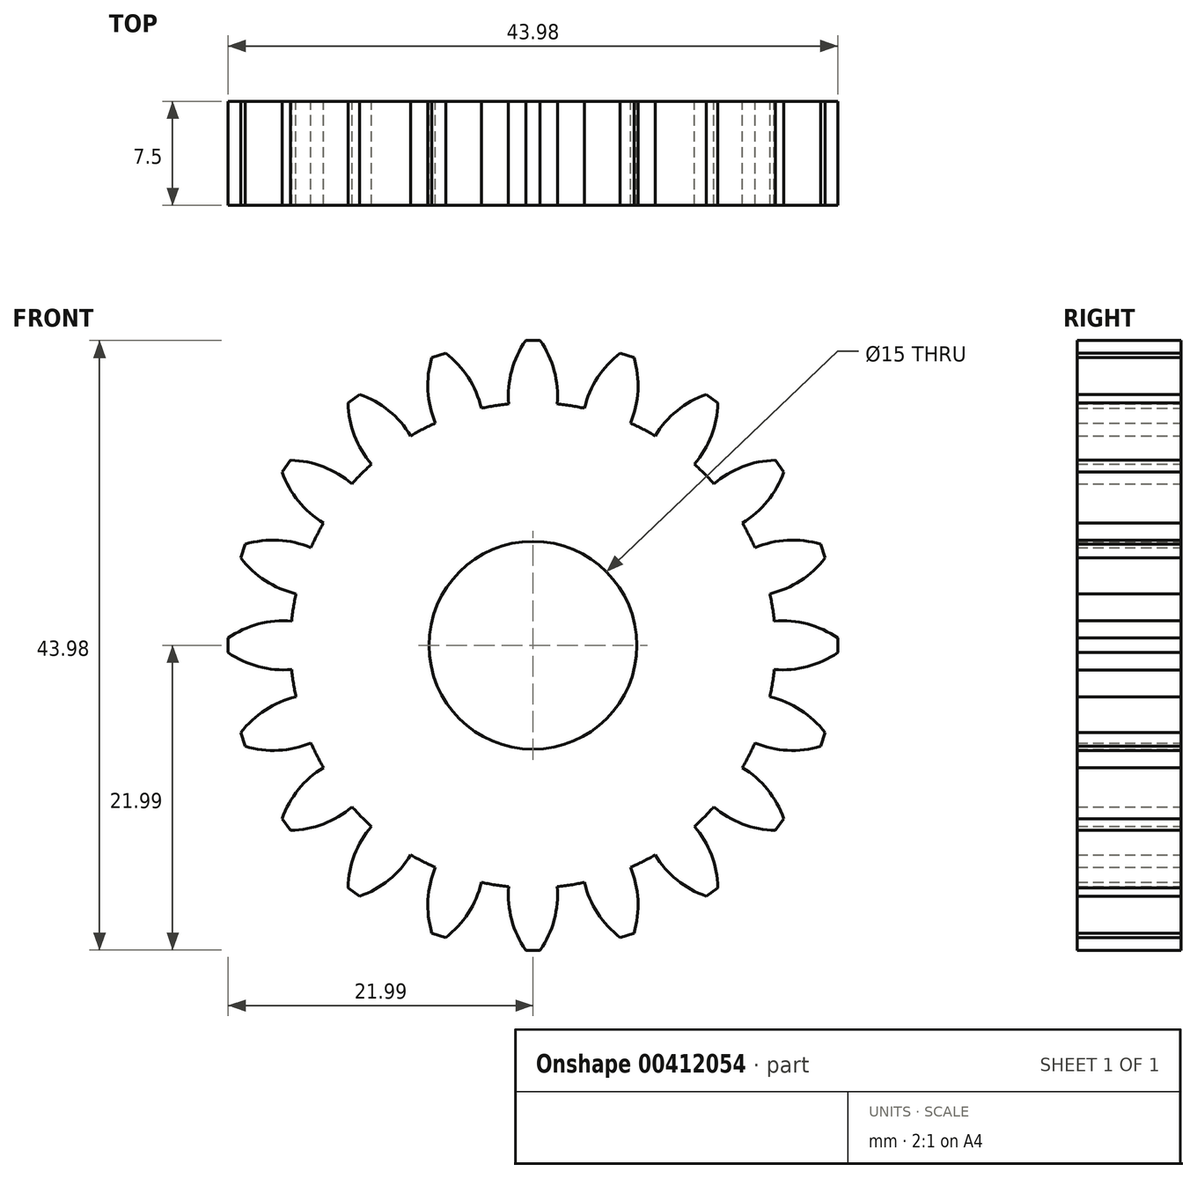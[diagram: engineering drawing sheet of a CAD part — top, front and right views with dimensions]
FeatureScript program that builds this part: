
annotation { "Feature Type Name" : "Feature", "Feature Type Description" : "" }
export const myFeature = defineFeature(function(context is Context, id is Id, definition is map)
    precondition{}
    {
        {
            var Q0;
            Q0=qCreatedBy(makeId("Front.planeOp"),FACE);
            var sketch = newSketch(context, id + "F0", { "sketchPlane" : qUnion([Q0])});
            skCircle(sketch, "E0", {"center": v(0, 0) * mm, "radius": 17.5 * mm});
            skCircle(sketch, "E1", {"center": v(0, 0) * mm, "radius": 22 * mm});
            skCircle(sketch, "E2", {"center": v(0, 0) * mm, "radius": 7.5 * mm});
            skLineSegment(sketch, "E3", {"start": v(-0.52, 22) * mm, "end": v(0.52, 22) * mm});
            skArc(sketch, "E4", {"start": v(-0.52, 22) * mm, "mid": v(-1.53, 19.81) * mm, "end": v(-1.75, 17.41) * mm});
            skArc(sketch, "E5.MirrorCS", {"start": v(0.52, 22) * mm, "mid": v(1.53, 19.81) * mm, "end": v(1.75, 17.41) * mm});
            skLineSegment(sketch, "E6.1.0", {"start": v(-7.3, 20.76) * mm, "end": v(-6.3, 21.08) * mm});
            skArc(sketch, "E6.1.1", {"start": v(-7.3, 20.76) * mm, "mid": v(-7.58, 18.37) * mm, "end": v(-7.04, 16.02) * mm});
            skArc(sketch, "E6.1.2", {"start": v(-6.3, 21.08) * mm, "mid": v(-4.66, 19.31) * mm, "end": v(-3.72, 17.1) * mm});
            skLineSegment(sketch, "E6.2.0", {"start": v(-13.35, 17.49) * mm, "end": v(-12.5, 18.1) * mm});
            skArc(sketch, "E6.2.1", {"start": v(-13.35, 17.49) * mm, "mid": v(-12.88, 15.13) * mm, "end": v(-11.65, 13.06) * mm});
            skArc(sketch, "E6.2.2", {"start": v(-12.5, 18.1) * mm, "mid": v(-10.4, 16.93) * mm, "end": v(-8.82, 15.11) * mm});
            skLineSegment(sketch, "E6.3.0", {"start": v(-18.1, 12.5) * mm, "end": v(-17.49, 13.35) * mm});
            skArc(sketch, "E6.3.1", {"start": v(-18.1, 12.5) * mm, "mid": v(-16.93, 10.4) * mm, "end": v(-15.11, 8.82) * mm});
            skArc(sketch, "E6.3.2", {"start": v(-17.49, 13.35) * mm, "mid": v(-15.13, 12.88) * mm, "end": v(-13.06, 11.65) * mm});
            skLineSegment(sketch, "E6.4.0", {"start": v(-21.08, 6.3) * mm, "end": v(-20.76, 7.3) * mm});
            skArc(sketch, "E6.4.1", {"start": v(-21.08, 6.3) * mm, "mid": v(-19.31, 4.66) * mm, "end": v(-17.1, 3.72) * mm});
            skArc(sketch, "E6.4.2", {"start": v(-20.76, 7.3) * mm, "mid": v(-18.37, 7.58) * mm, "end": v(-16.02, 7.04) * mm});
            skLineSegment(sketch, "E6.5.0", {"start": v(-22, -0.52) * mm, "end": v(-22, 0.52) * mm});
            skArc(sketch, "E6.5.1", {"start": v(-22, -0.52) * mm, "mid": v(-19.81, -1.53) * mm, "end": v(-17.41, -1.75) * mm});
            skArc(sketch, "E6.5.2", {"start": v(-22, 0.52) * mm, "mid": v(-19.81, 1.53) * mm, "end": v(-17.41, 1.75) * mm});
            skLineSegment(sketch, "E6.6.0", {"start": v(-20.76, -7.3) * mm, "end": v(-21.08, -6.3) * mm});
            skArc(sketch, "E6.6.1", {"start": v(-20.76, -7.3) * mm, "mid": v(-18.37, -7.58) * mm, "end": v(-16.02, -7.04) * mm});
            skArc(sketch, "E6.6.2", {"start": v(-21.08, -6.3) * mm, "mid": v(-19.31, -4.66) * mm, "end": v(-17.1, -3.72) * mm});
            skLineSegment(sketch, "E6.7.0", {"start": v(-17.49, -13.35) * mm, "end": v(-18.1, -12.5) * mm});
            skArc(sketch, "E6.7.1", {"start": v(-17.49, -13.35) * mm, "mid": v(-15.13, -12.88) * mm, "end": v(-13.06, -11.65) * mm});
            skArc(sketch, "E6.7.2", {"start": v(-18.1, -12.5) * mm, "mid": v(-16.93, -10.4) * mm, "end": v(-15.11, -8.82) * mm});
            skLineSegment(sketch, "E6.8.0", {"start": v(-12.5, -18.1) * mm, "end": v(-13.35, -17.49) * mm});
            skArc(sketch, "E6.8.1", {"start": v(-12.5, -18.1) * mm, "mid": v(-10.4, -16.93) * mm, "end": v(-8.82, -15.11) * mm});
            skArc(sketch, "E6.8.2", {"start": v(-13.35, -17.49) * mm, "mid": v(-12.88, -15.13) * mm, "end": v(-11.65, -13.06) * mm});
            skLineSegment(sketch, "E6.9.0", {"start": v(-6.3, -21.08) * mm, "end": v(-7.3, -20.76) * mm});
            skArc(sketch, "E6.9.1", {"start": v(-6.3, -21.08) * mm, "mid": v(-4.66, -19.31) * mm, "end": v(-3.72, -17.1) * mm});
            skArc(sketch, "E6.9.2", {"start": v(-7.3, -20.76) * mm, "mid": v(-7.58, -18.37) * mm, "end": v(-7.04, -16.02) * mm});
            skLineSegment(sketch, "E6.10.0", {"start": v(0.52, -22) * mm, "end": v(-0.52, -22) * mm});
            skArc(sketch, "E6.10.1", {"start": v(0.52, -22) * mm, "mid": v(1.53, -19.81) * mm, "end": v(1.75, -17.41) * mm});
            skArc(sketch, "E6.10.2", {"start": v(-0.52, -22) * mm, "mid": v(-1.53, -19.81) * mm, "end": v(-1.75, -17.41) * mm});
            skLineSegment(sketch, "E6.11.0", {"start": v(7.3, -20.76) * mm, "end": v(6.3, -21.08) * mm});
            skArc(sketch, "E6.11.1", {"start": v(7.3, -20.76) * mm, "mid": v(7.58, -18.37) * mm, "end": v(7.04, -16.02) * mm});
            skArc(sketch, "E6.11.2", {"start": v(6.3, -21.08) * mm, "mid": v(4.66, -19.31) * mm, "end": v(3.72, -17.1) * mm});
            skLineSegment(sketch, "E6.12.0", {"start": v(13.35, -17.49) * mm, "end": v(12.5, -18.1) * mm});
            skArc(sketch, "E6.12.1", {"start": v(13.35, -17.49) * mm, "mid": v(12.88, -15.13) * mm, "end": v(11.65, -13.06) * mm});
            skArc(sketch, "E6.12.2", {"start": v(12.5, -18.1) * mm, "mid": v(10.4, -16.93) * mm, "end": v(8.82, -15.11) * mm});
            skLineSegment(sketch, "E6.13.0", {"start": v(18.1, -12.5) * mm, "end": v(17.49, -13.35) * mm});
            skArc(sketch, "E6.13.1", {"start": v(18.1, -12.5) * mm, "mid": v(16.93, -10.4) * mm, "end": v(15.11, -8.82) * mm});
            skArc(sketch, "E6.13.2", {"start": v(17.49, -13.35) * mm, "mid": v(15.13, -12.88) * mm, "end": v(13.06, -11.65) * mm});
            skLineSegment(sketch, "E6.14.0", {"start": v(21.08, -6.3) * mm, "end": v(20.76, -7.3) * mm});
            skArc(sketch, "E6.14.1", {"start": v(21.08, -6.3) * mm, "mid": v(19.31, -4.66) * mm, "end": v(17.1, -3.72) * mm});
            skArc(sketch, "E6.14.2", {"start": v(20.76, -7.3) * mm, "mid": v(18.37, -7.58) * mm, "end": v(16.02, -7.04) * mm});
            skLineSegment(sketch, "E6.15.0", {"start": v(22, 0.52) * mm, "end": v(22, -0.52) * mm});
            skArc(sketch, "E6.15.1", {"start": v(22, 0.52) * mm, "mid": v(19.81, 1.53) * mm, "end": v(17.41, 1.75) * mm});
            skArc(sketch, "E6.15.2", {"start": v(22, -0.52) * mm, "mid": v(19.81, -1.53) * mm, "end": v(17.41, -1.75) * mm});
            skLineSegment(sketch, "E6.16.0", {"start": v(20.76, 7.3) * mm, "end": v(21.08, 6.3) * mm});
            skArc(sketch, "E6.16.1", {"start": v(20.76, 7.3) * mm, "mid": v(18.37, 7.58) * mm, "end": v(16.02, 7.04) * mm});
            skArc(sketch, "E6.16.2", {"start": v(21.08, 6.3) * mm, "mid": v(19.31, 4.66) * mm, "end": v(17.1, 3.72) * mm});
            skLineSegment(sketch, "E6.17.0", {"start": v(17.49, 13.35) * mm, "end": v(18.1, 12.5) * mm});
            skArc(sketch, "E6.17.1", {"start": v(17.49, 13.35) * mm, "mid": v(15.13, 12.88) * mm, "end": v(13.06, 11.65) * mm});
            skArc(sketch, "E6.17.2", {"start": v(18.1, 12.5) * mm, "mid": v(16.93, 10.4) * mm, "end": v(15.11, 8.82) * mm});
            skLineSegment(sketch, "E6.18.0", {"start": v(12.5, 18.1) * mm, "end": v(13.35, 17.49) * mm});
            skArc(sketch, "E6.18.1", {"start": v(12.5, 18.1) * mm, "mid": v(10.4, 16.93) * mm, "end": v(8.82, 15.11) * mm});
            skArc(sketch, "E6.18.2", {"start": v(13.35, 17.49) * mm, "mid": v(12.88, 15.13) * mm, "end": v(11.65, 13.06) * mm});
            skLineSegment(sketch, "E6.19.0", {"start": v(6.3, 21.08) * mm, "end": v(7.3, 20.76) * mm});
            skArc(sketch, "E6.19.1", {"start": v(6.3, 21.08) * mm, "mid": v(4.66, 19.31) * mm, "end": v(3.72, 17.1) * mm});
            skArc(sketch, "E6.19.2", {"start": v(7.3, 20.76) * mm, "mid": v(7.58, 18.37) * mm, "end": v(7.04, 16.02) * mm});
            skSolve(sketch);
        }
        {
            var Q0;
            Q0=makeQuery(id+"F0.imprint","IMPRINT",FACE,{"disambiguationData":[TD([[makeQuery(id+"F0.imprint","IMPRINT",EDGE,{"derivedFrom":sQuery(id+"F0.wireOp",EDGE,"E3")}),-1.0]])]});
            var Q1;
            Q1=makeQuery(id+"F0.imprint","IMPRINT",FACE,{"disambiguationData":[TD([[makeQuery(id+"F0.imprint","IMPRINT",EDGE,{"derivedFrom":sQuery(id+"F0.wireOp",EDGE,"E2")}),-1.0]])]});
            var Q2;
            Q2=makeQuery(id+"F0.imprint","IMPRINT",FACE,{"disambiguationData":[TD([[makeQuery(id+"F0.imprint","IMPRINT",EDGE,{"derivedFrom":sQuery(id+"F0.wireOp",EDGE,"E6.1.0")}),-1.0]])]});
            var Q3;
            Q3=makeQuery(id+"F0.imprint","IMPRINT",FACE,{"disambiguationData":[TD([[makeQuery(id+"F0.imprint","IMPRINT",EDGE,{"derivedFrom":sQuery(id+"F0.wireOp",EDGE,"E6.2.0")}),-1.0]])]});
            var Q4;
            Q4=makeQuery(id+"F0.imprint","IMPRINT",FACE,{"disambiguationData":[TD([[makeQuery(id+"F0.imprint","IMPRINT",EDGE,{"derivedFrom":sQuery(id+"F0.wireOp",EDGE,"E6.3.0")}),-1.0]])]});
            var Q5;
            Q5=makeQuery(id+"F0.imprint","IMPRINT",FACE,{"disambiguationData":[TD([[makeQuery(id+"F0.imprint","IMPRINT",EDGE,{"derivedFrom":sQuery(id+"F0.wireOp",EDGE,"E6.4.0")}),-1.0]])]});
            var Q6;
            Q6=makeQuery(id+"F0.imprint","IMPRINT",FACE,{"disambiguationData":[TD([[makeQuery(id+"F0.imprint","IMPRINT",EDGE,{"derivedFrom":sQuery(id+"F0.wireOp",EDGE,"E6.5.0")}),-1.0]])]});
            var Q7;
            Q7=makeQuery(id+"F0.imprint","IMPRINT",FACE,{"disambiguationData":[TD([[makeQuery(id+"F0.imprint","IMPRINT",EDGE,{"derivedFrom":sQuery(id+"F0.wireOp",EDGE,"E6.6.0")}),-1.0]])]});
            var Q8;
            Q8=makeQuery(id+"F0.imprint","IMPRINT",FACE,{"disambiguationData":[TD([[makeQuery(id+"F0.imprint","IMPRINT",EDGE,{"derivedFrom":sQuery(id+"F0.wireOp",EDGE,"E6.7.0")}),-1.0]])]});
            var Q9;
            Q9=makeQuery(id+"F0.imprint","IMPRINT",FACE,{"disambiguationData":[TD([[makeQuery(id+"F0.imprint","IMPRINT",EDGE,{"derivedFrom":sQuery(id+"F0.wireOp",EDGE,"E6.8.0")}),-1.0]])]});
            var Q10;
            Q10=makeQuery(id+"F0.imprint","IMPRINT",FACE,{"disambiguationData":[TD([[makeQuery(id+"F0.imprint","IMPRINT",EDGE,{"derivedFrom":sQuery(id+"F0.wireOp",EDGE,"E6.9.0")}),-1.0]])]});
            var Q11;
            Q11=makeQuery(id+"F0.imprint","IMPRINT",FACE,{"disambiguationData":[TD([[makeQuery(id+"F0.imprint","IMPRINT",EDGE,{"derivedFrom":sQuery(id+"F0.wireOp",EDGE,"E6.10.0")}),-1.0]])]});
            var Q12;
            Q12=makeQuery(id+"F0.imprint","IMPRINT",FACE,{"disambiguationData":[TD([[makeQuery(id+"F0.imprint","IMPRINT",EDGE,{"derivedFrom":sQuery(id+"F0.wireOp",EDGE,"E6.11.0")}),-1.0]])]});
            var Q13;
            Q13=makeQuery(id+"F0.imprint","IMPRINT",FACE,{"disambiguationData":[TD([[makeQuery(id+"F0.imprint","IMPRINT",EDGE,{"derivedFrom":sQuery(id+"F0.wireOp",EDGE,"E6.12.0")}),-1.0]])]});
            var Q14;
            Q14=makeQuery(id+"F0.imprint","IMPRINT",FACE,{"disambiguationData":[TD([[makeQuery(id+"F0.imprint","IMPRINT",EDGE,{"derivedFrom":sQuery(id+"F0.wireOp",EDGE,"E6.14.0")}),-1.0]])]});
            var Q15;
            Q15=makeQuery(id+"F0.imprint","IMPRINT",FACE,{"disambiguationData":[TD([[makeQuery(id+"F0.imprint","IMPRINT",EDGE,{"derivedFrom":sQuery(id+"F0.wireOp",EDGE,"E6.15.0")}),-1.0]])]});
            var Q16;
            Q16=makeQuery(id+"F0.imprint","IMPRINT",FACE,{"disambiguationData":[TD([[makeQuery(id+"F0.imprint","IMPRINT",EDGE,{"derivedFrom":sQuery(id+"F0.wireOp",EDGE,"E6.13.0")}),-1.0]])]});
            var Q17;
            Q17=makeQuery(id+"F0.imprint","IMPRINT",FACE,{"disambiguationData":[TD([[makeQuery(id+"F0.imprint","IMPRINT",EDGE,{"derivedFrom":sQuery(id+"F0.wireOp",EDGE,"E6.16.0")}),-1.0]])]});
            var Q18;
            Q18=makeQuery(id+"F0.imprint","IMPRINT",FACE,{"disambiguationData":[TD([[makeQuery(id+"F0.imprint","IMPRINT",EDGE,{"derivedFrom":sQuery(id+"F0.wireOp",EDGE,"E6.17.0")}),-1.0]])]});
            var Q19;
            Q19=makeQuery(id+"F0.imprint","IMPRINT",FACE,{"disambiguationData":[TD([[makeQuery(id+"F0.imprint","IMPRINT",EDGE,{"derivedFrom":sQuery(id+"F0.wireOp",EDGE,"E6.18.0")}),-1.0]])]});
            var Q20;
            Q20=makeQuery(id+"F0.imprint","IMPRINT",FACE,{"disambiguationData":[TD([[makeQuery(id+"F0.imprint","IMPRINT",EDGE,{"derivedFrom":sQuery(id+"F0.wireOp",EDGE,"E6.19.0")}),-1.0]])]});
            extrude(context, id + "F1", {"entities" : qUnion([Q0, Q1, Q2, Q3, Q4, Q5, Q6, Q7, Q8, Q9, Q10, Q11, Q12, Q13, Q14, Q15, Q16, Q17, Q18, Q19, Q20]), "depth" : 7.5 * mm});
        }
    });
